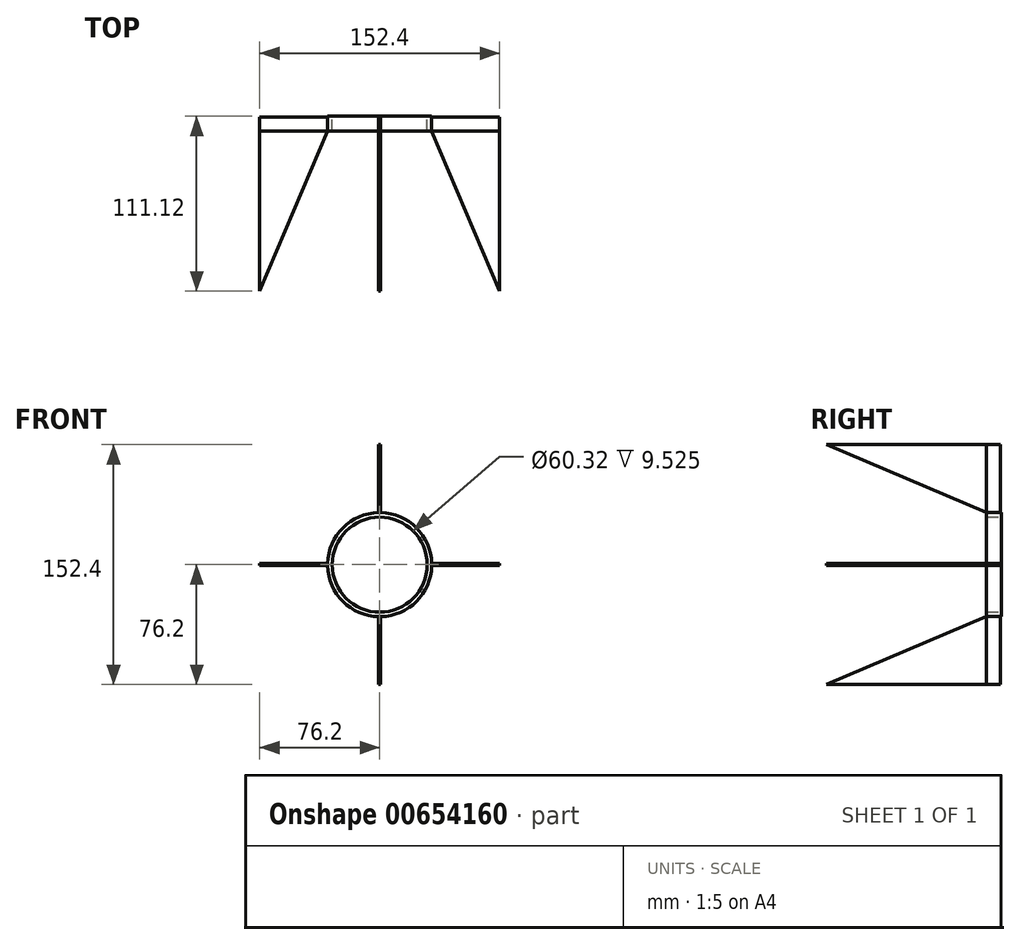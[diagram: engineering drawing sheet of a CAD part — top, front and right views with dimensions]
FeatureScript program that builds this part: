
annotation { "Feature Type Name" : "Feature", "Feature Type Description" : "" }
export const myFeature = defineFeature(function(context is Context, id is Id, definition is map)
    precondition{}
    {
        {
            var Q0;
            Q0=qCreatedBy(makeId("Front.planeOp"),FACE);
            var sketch = newSketch(context, id + "F0", { "sketchPlane" : qUnion([Q0])});
            skCircle(sketch, "E0", {"center": v(0, 0) * mm, "radius": 33.02 * mm});
            skCircle(sketch, "E1", {"center": v(0, 0) * mm, "radius": 30.16 * mm});
            skSolve(sketch);
        }
        {
            var Q0;
            Q0=makeQuery(id+"F0.imprint","IMPRINT",FACE,{"disambiguationData":[TD([[makeQuery(id+"F0.imprint","IMPRINT",EDGE,{"derivedFrom":sQuery(id+"F0.wireOp",EDGE,"E0")}),1.0]])]});
            extrude(context, id + "F1", {"entities" : qUnion([Q0]), "depth" : 9.52 * mm, "offsetDistance" : 25.4 * mm});
        }
        {
            var Q0;
            Q0=makeQuery(id+"F1.opExtrude","CAP_FACE",FACE,{"disambiguationData":[OSD([sQuery(id+"F0.wireOp",EDGE,"E0"),sQuery(id+"F0.wireOp",EDGE,"E1")])],"isStart":false});
            var sketch = newSketch(context, id + "F2", { "sketchPlane" : qUnion([Q0])});
            skSolve(sketch);
        }
        {
            var Q0;
            Q0=makeQuery(id+"F2.imprint","IMPRINT",FACE,{"disambiguationData":[TD([[makeQuery(id+"F2.imprint","IMPRINT",EDGE,{"derivedFrom":makeQuery(id+"F1.opExtrude","CAP_EDGE",EDGE,{"disambiguationData":[OSD([sQuery(id+"F0.wireOp",EDGE,"E0")])],"isStart":false})}),1.0]])]});
            var sketch = newSketch(context, id + "F3", { "sketchPlane" : qUnion([Q0])});
            skLineSegment(sketch, "E2.bottom", {"start": v(-0.63, 76.2) * mm, "end": v(0.64, 76.2) * mm});
            skLineSegment(sketch, "E2.top", {"start": v(-0.64, -76.2) * mm, "end": v(0.63, -76.2) * mm});
            skLineSegment(sketch, "E2.left", {"start": v(-0.63, 76.2) * mm, "end": v(-0.63, 0.63) * mm});
            skLineSegment(sketch, "E2.right", {"start": v(0.64, 76.2) * mm, "end": v(0.64, 0.63) * mm});
            skPoint(sketch, "E2.middle", {"position": v(0, 0) * mm});
            skLineSegment(sketch, "E3.bottom", {"start": v(-76.2, 0.63) * mm, "end": v(-0.63, 0.63) * mm});
            skLineSegment(sketch, "E3.top", {"start": v(-76.2, -0.63) * mm, "end": v(-0.63, -0.63) * mm});
            skLineSegment(sketch, "E3.left", {"start": v(-76.2, 0.63) * mm, "end": v(-76.2, -0.63) * mm});
            skLineSegment(sketch, "E3.right", {"start": v(76.2, 0.63) * mm, "end": v(76.2, -0.63) * mm});
            skLineSegment(sketch, "E4.trimOffspring", {"start": v(0.64, -0.63) * mm, "end": v(0.63, -76.2) * mm});
            skLineSegment(sketch, "E5.trimOffspring", {"start": v(-0.63, -0.63) * mm, "end": v(-0.64, -76.2) * mm});
            skLineSegment(sketch, "E6.trimOffspring", {"start": v(0.63, -0.63) * mm, "end": v(76.2, -0.63) * mm});
            skLineSegment(sketch, "E7.trimOffspring", {"start": v(0.63, 0.63) * mm, "end": v(76.2, 0.63) * mm});
            skSolve(sketch);
        }
        {
            var Q0;
            {var subQ0=sQuery(id+"F3.wireOp",EDGE,"E2.top");Q0=makeQuery(id+"F3.imprint","IMPRINT",FACE,{"disambiguationData":[TD([[makeQuery(id+"F3.imprint","IMPRINT",EDGE,{"derivedFrom":subQ0}),1.0]])]});}
            var Q1;
            {var subQ0=sQuery(id+"F3.wireOp",EDGE,"E2.bottom");Q1=makeQuery(id+"F3.imprint","IMPRINT",FACE,{"disambiguationData":[TD([[makeQuery(id+"F3.imprint","IMPRINT",EDGE,{"derivedFrom":subQ0}),-1.0]])]});}
            var Q2;
            {var subQ0=sQuery(id+"F3.wireOp",EDGE,"E3.left");Q2=makeQuery(id+"F3.imprint","IMPRINT",FACE,{"disambiguationData":[TD([[makeQuery(id+"F3.imprint","IMPRINT",EDGE,{"derivedFrom":subQ0}),1.0]])]});}
            var Q3;
            {var subQ0=sQuery(id+"F3.wireOp",EDGE,"E3.right");Q3=makeQuery(id+"F3.imprint","IMPRINT",FACE,{"disambiguationData":[TD([[makeQuery(id+"F3.imprint","IMPRINT",EDGE,{"derivedFrom":subQ0}),-1.0]])]});}
            extrude(context, id + "F4", {"entities" : qUnion([Q0, Q1, Q2, Q3]), "depth" : 101.6 * mm, "offsetDistance" : 25.4 * mm});
        }
        {
            var Q0;
            Q0=makeQuery(id+"F4.opExtrude","CAP_FACE",FACE,{"disambiguationData":[OSD([sQuery(id+"F0.wireOp",EDGE,"E0"),sQuery(id+"F3.wireOp",EDGE,"E2.bottom"),sQuery(id+"F3.wireOp",EDGE,"E2.left"),sQuery(id+"F3.wireOp",EDGE,"E2.right")])],"isStart":true});
            var Q1;
            Q1=makeQuery(id+"F4.opExtrude","CAP_FACE",FACE,{"disambiguationData":[OSD([sQuery(id+"F0.wireOp",EDGE,"E0"),sQuery(id+"F3.wireOp",EDGE,"E3.bottom"),sQuery(id+"F3.wireOp",EDGE,"E3.top"),sQuery(id+"F3.wireOp",EDGE,"E3.left")])],"isStart":true});
            var Q2;
            Q2=makeQuery(id+"F4.opExtrude","CAP_FACE",FACE,{"disambiguationData":[OSD([sQuery(id+"F0.wireOp",EDGE,"E0"),sQuery(id+"F3.wireOp",EDGE,"E2.top"),sQuery(id+"F3.wireOp",EDGE,"E4.trimOffspring"),sQuery(id+"F3.wireOp",EDGE,"E5.trimOffspring")])],"isStart":true});
            var Q3;
            Q3=makeQuery(id+"F4.opExtrude","CAP_FACE",FACE,{"disambiguationData":[OSD([sQuery(id+"F0.wireOp",EDGE,"E0"),sQuery(id+"F3.wireOp",EDGE,"E3.right"),sQuery(id+"F3.wireOp",EDGE,"E6.trimOffspring"),sQuery(id+"F3.wireOp",EDGE,"E7.trimOffspring")])],"isStart":true});
            extrude(context, id + "F5", {"entities" : qUnion([Q0, Q1, Q2, Q3]), "depth" : 8.9 * mm, "offsetDistance" : 25.4 * mm});
        }
        {
            var Q0;
            Q0=makeQuery(id+"F4.opExtrude","SWEPT_FACE",FACE,{"disambiguationData":[OSD([sQuery(id+"F3.wireOp",EDGE,"E2.left")])]});
            var sketch = newSketch(context, id + "F6", { "sketchPlane" : qUnion([Q0])});
            skLineSegment(sketch, "E8", {"start": v(9.52, 33.01) * mm, "end": v(111.13, 76.2) * mm});
            skSolve(sketch);
        }
        {
            var Q0;
            Q0=makeQuery(id+"F6.imprint","IMPRINT",FACE,{"disambiguationData":[TD([[makeQuery(id+"F6.imprint","IMPRINT",EDGE,{"derivedFrom":sQuery(id+"F6.wireOp",EDGE,"E8")}),-1.0]])]});
            extrude(context, id + "F7", {"entities" : qUnion([Q0]), "operationType" : NewBodyOperationType.REMOVE, "oppositeDirection" : true, "depth" : 25.4 * mm, "offsetDistance" : 25.4 * mm});
        }
        {
            var Q0;
            Q0=makeQuery(id+"F4.opExtrude","SWEPT_FACE",FACE,{"disambiguationData":[OSD([sQuery(id+"F3.wireOp",EDGE,"E3.bottom")])]});
            var sketch = newSketch(context, id + "F8", { "sketchPlane" : qUnion([Q0])});
            skLineSegment(sketch, "E9", {"start": v(-33.01, -9.52) * mm, "end": v(-76.2, -111.13) * mm});
            skSolve(sketch);
        }
        {
            var Q0;
            Q0=makeQuery(id+"F8.imprint","IMPRINT",FACE,{"disambiguationData":[TD([[makeQuery(id+"F8.imprint","IMPRINT",EDGE,{"derivedFrom":sQuery(id+"F8.wireOp",EDGE,"E9")}),1.0]])]});
            extrude(context, id + "F9", {"entities" : qUnion([Q0]), "operationType" : NewBodyOperationType.REMOVE, "oppositeDirection" : true, "depth" : 25.4 * mm, "offsetDistance" : 25.4 * mm});
        }
        {
            var Q0;
            Q0=makeQuery(id+"F4.opExtrude","SWEPT_FACE",FACE,{"disambiguationData":[OSD([sQuery(id+"F3.wireOp",EDGE,"E6.trimOffspring")])]});
            var sketch = newSketch(context, id + "F10", { "sketchPlane" : qUnion([Q0])});
            skLineSegment(sketch, "E10", {"start": v(33.01, 9.52) * mm, "end": v(76.2, 111.13) * mm});
            skSolve(sketch);
        }
        {
            var Q0;
            Q0=makeQuery(id+"F10.imprint","IMPRINT",FACE,{"disambiguationData":[TD([[makeQuery(id+"F10.imprint","IMPRINT",EDGE,{"derivedFrom":sQuery(id+"F10.wireOp",EDGE,"E10")}),1.0]])]});
            extrude(context, id + "F11", {"entities" : qUnion([Q0]), "operationType" : NewBodyOperationType.REMOVE, "oppositeDirection" : true, "depth" : 25.4 * mm, "offsetDistance" : 25.4 * mm});
        }
        {
            var Q0;
            Q0=makeQuery(id+"F4.opExtrude","SWEPT_FACE",FACE,{"disambiguationData":[OSD([sQuery(id+"F3.wireOp",EDGE,"E4.trimOffspring")])]});
            var sketch = newSketch(context, id + "F12", { "sketchPlane" : qUnion([Q0])});
            skLineSegment(sketch, "E11", {"start": v(-9.52, -33.01) * mm, "end": v(-111.13, -76.2) * mm});
            skSolve(sketch);
        }
        {
            var Q0;
            Q0=makeQuery(id+"F12.imprint","IMPRINT",FACE,{"disambiguationData":[TD([[makeQuery(id+"F12.imprint","IMPRINT",EDGE,{"derivedFrom":sQuery(id+"F12.wireOp",EDGE,"E11")}),-1.0]])]});
            extrude(context, id + "F13", {"entities" : qUnion([Q0]), "operationType" : NewBodyOperationType.REMOVE, "oppositeDirection" : true, "depth" : 25.4 * mm, "offsetDistance" : 25.4 * mm});
        }
    });
